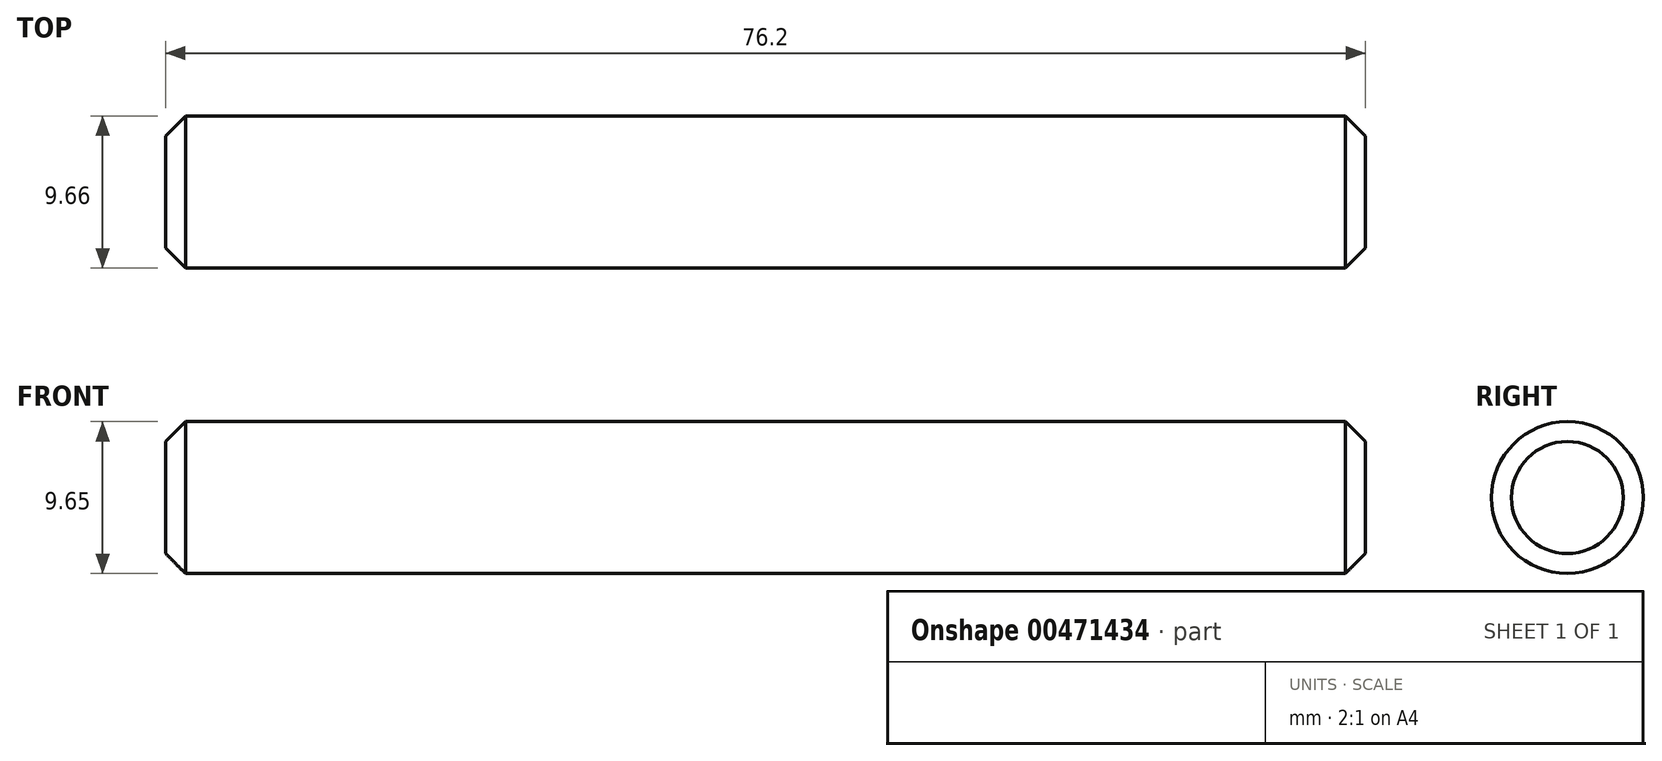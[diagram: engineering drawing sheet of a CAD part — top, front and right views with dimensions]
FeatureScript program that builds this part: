
annotation { "Feature Type Name" : "Feature", "Feature Type Description" : "" }
export const myFeature = defineFeature(function(context is Context, id is Id, definition is map)
    precondition{}
    {
        {
            var Q0;
            Q0=qCreatedBy(makeId("Front.planeOp"),FACE);
            var sketch = newSketch(context, id + "F0", { "sketchPlane" : qUnion([Q0])});
            skLineSegment(sketch, "E0.bottom", {"start": v(0, 0) * mm, "end": v(76.2, 0) * mm});
            skLineSegment(sketch, "E0.top", {"start": v(0, -4.83) * mm, "end": v(76.2, -4.83) * mm});
            skLineSegment(sketch, "E0.left", {"start": v(0, 0) * mm, "end": v(0, -4.83) * mm});
            skLineSegment(sketch, "E0.right", {"start": v(76.2, 0) * mm, "end": v(76.2, -4.83) * mm});
            skSolve(sketch);
        }
        {
            var Q0;
            Q0 = qSketchRegion(id + "F0", true);
            var Q1;
            Q1=sQuery(id+"F0.wireOp",EDGE,"E0.top");
            revolve(context, id + "F1", {"entities" : qUnion([Q0]), "axis" : qUnion([Q1]), "revolveType" : RevolveType.FULL});
        }
        {
            var Q0;
            Q0=makeQuery(id+"F1.opRevolve","SWEPT_EDGE",EDGE,{"disambiguationData":[OSD([sQuery(id+"F0.wireOp",EDGE,"E0.bottom"),sQuery(id+"F0.wireOp",EDGE,"E0.left")])]});
            chamfer(context, id + "F2", {"entities" : qUnion([Q0]), "width" : 1.27 * mm, "tangentPropagation" : true});
        }
        {
            var Q0;
            Q0=makeQuery(id+"F1.opRevolve","SWEPT_EDGE",EDGE,{"disambiguationData":[OSD([sQuery(id+"F0.wireOp",EDGE,"E0.bottom"),sQuery(id+"F0.wireOp",EDGE,"E0.right")])]});
            chamfer(context, id + "F3", {"entities" : qUnion([Q0]), "width" : 1.27 * mm, "tangentPropagation" : true});
        }
    });
